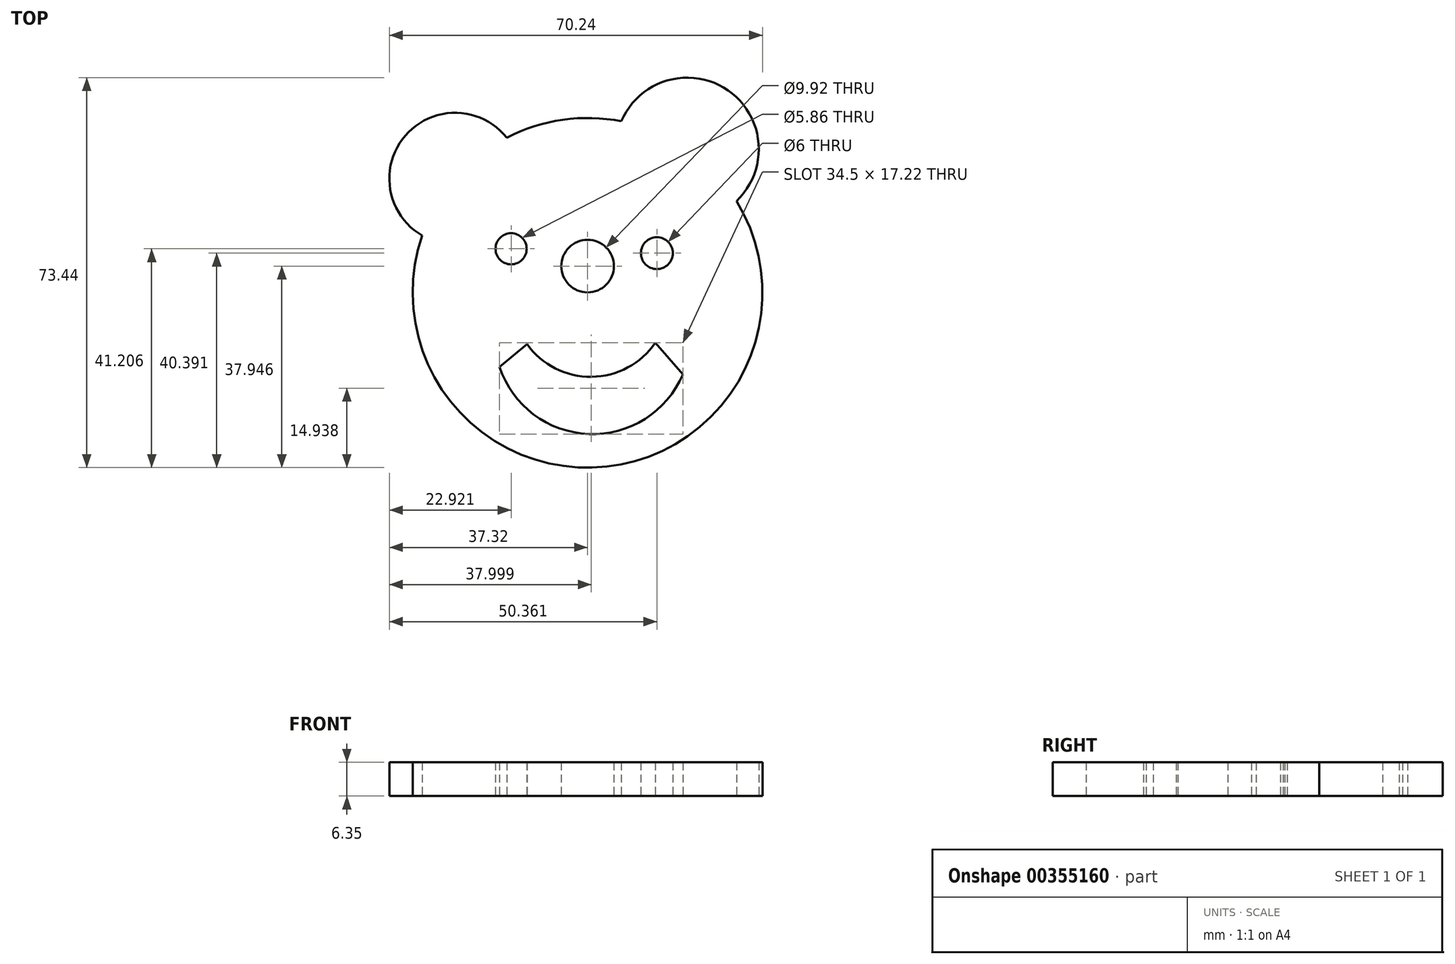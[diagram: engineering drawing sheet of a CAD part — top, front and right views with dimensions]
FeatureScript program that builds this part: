
annotation { "Feature Type Name" : "Feature", "Feature Type Description" : "" }
export const myFeature = defineFeature(function(context is Context, id is Id, definition is map)
    precondition{}
    {
        {
            var Q0;
            Q0=qCreatedBy(makeId("Top.planeOp"),FACE);
            var sketch = newSketch(context, id + "F0", { "sketchPlane" : qUnion([Q0])});
            skCircle(sketch, "E0", {"center": v(0, 0) * mm, "radius": 32.92 * mm});
            skCircle(sketch, "E1", {"center": v(18.76, 27.05) * mm, "radius": 13.46 * mm});
            skCircle(sketch, "E2", {"center": v(-24.92, 21.51) * mm, "radius": 12.4 * mm});
            skCircle(sketch, "E3", {"center": v(0, 5.03) * mm, "radius": 4.96 * mm});
            skArc(sketch, "E4", {"start": v(-16.57, -14) * mm, "mid": v(0.2, -26.6) * mm, "end": v(17.93, -15.35) * mm});
            skArc(sketch, "E5", {"start": v(-11.41, -9.64) * mm, "mid": v(0.75, -15.82) * mm, "end": v(12.77, -9.37) * mm});
            skLineSegment(sketch, "E6", {"start": v(-16.57, -14) * mm, "end": v(-11.41, -9.64) * mm});
            skLineSegment(sketch, "E7", {"start": v(12.77, -9.37) * mm, "end": v(17.93, -15.35) * mm});
            skCircle(sketch, "E8", {"center": v(-14.4, 8.29) * mm, "radius": 2.93 * mm});
            skCircle(sketch, "E9", {"center": v(13.04, 7.47) * mm, "radius": 3 * mm});
            skSolve(sketch);
        }
        {
            var Q0;
            Q0 = qSketchRegion(id + "F0", true);
            extrude(context, id + "F1", {"entities" : qUnion([Q0]), "depth" : 6.35 * mm});
        }
    });
